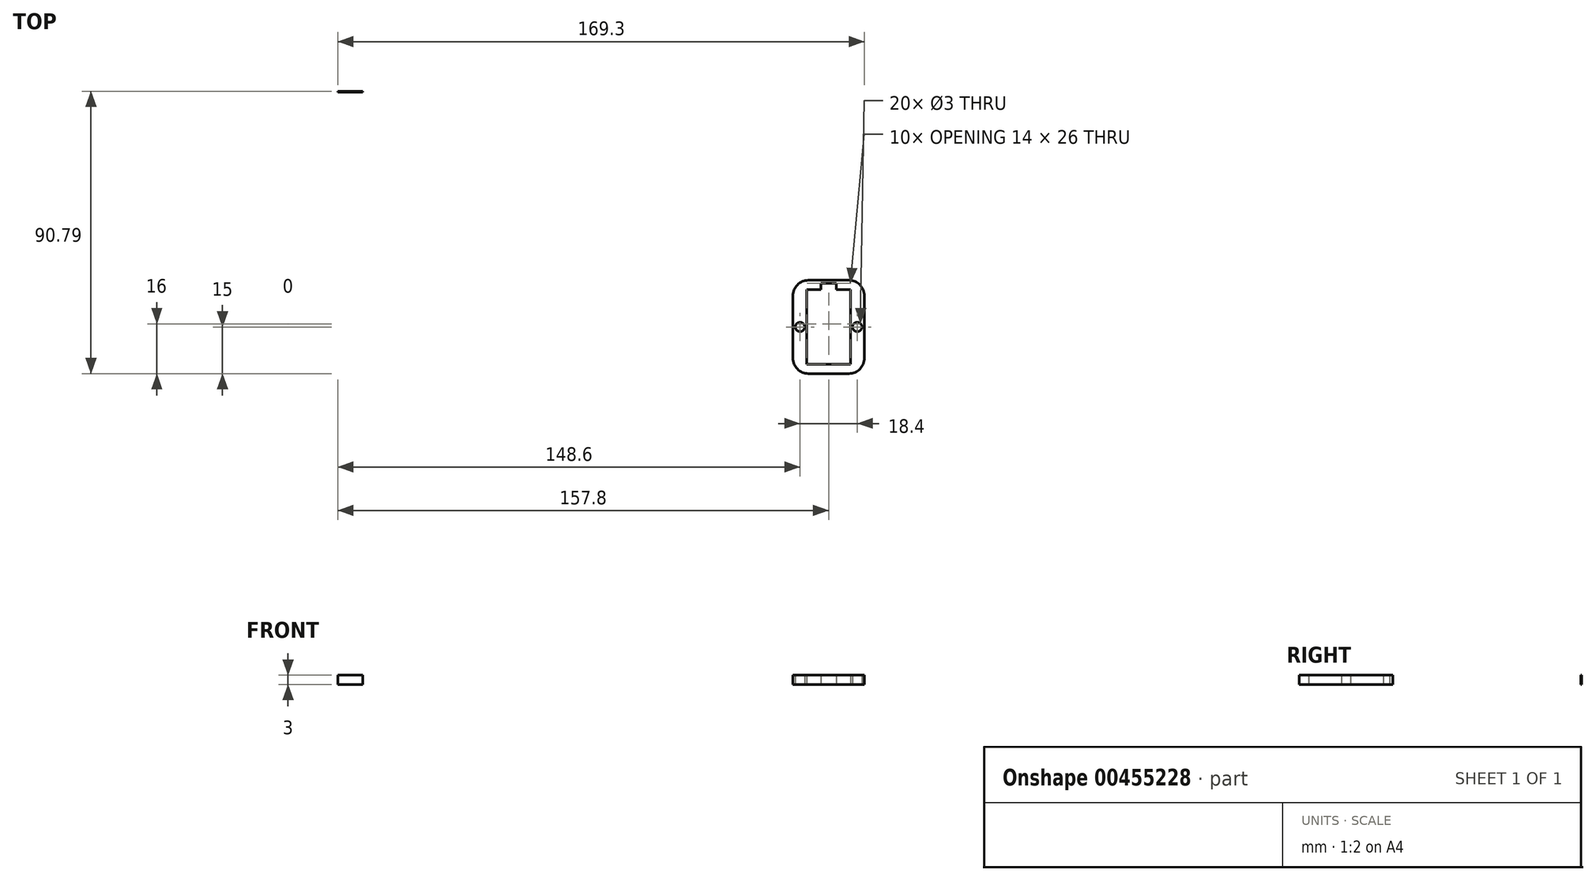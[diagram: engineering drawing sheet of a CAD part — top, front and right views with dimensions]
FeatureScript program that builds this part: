
annotation { "Feature Type Name" : "Feature", "Feature Type Description" : "" }
export const myFeature = defineFeature(function(context is Context, id is Id, definition is map)
    precondition{}
    {
        {
            var Q0;
            Q0=qCreatedBy(makeId("Top.planeOp"),FACE);
            var sketch = newSketch(context, id + "F0", { "sketchPlane" : qUnion([Q0])});
            skLineSegment(sketch, "E0.bottom", {"start": v(-157.8, 75.5) * mm, "end": v(-149.8, 75.5) * mm});
            skLineSegment(sketch, "E0.top", {"start": v(-157.8, 75.79) * mm, "end": v(-149.8, 75.79) * mm});
            skLineSegment(sketch, "E0.left", {"start": v(-157.8, 75.5) * mm, "end": v(-157.8, 75.79) * mm});
            skLineSegment(sketch, "E0.right", {"start": v(-149.8, 75.5) * mm, "end": v(-149.8, 75.79) * mm});
            skLineSegment(sketch, "E1.bottom", {"start": v(6.5, 15) * mm, "end": v(-6.5, 15) * mm});
            skLineSegment(sketch, "E1.top", {"start": v(6.5, -15) * mm, "end": v(-6.5, -15) * mm});
            skLineSegment(sketch, "E1.left", {"start": v(11.5, 10) * mm, "end": v(11.5, -10) * mm});
            skLineSegment(sketch, "E1.right", {"start": v(-11.5, 10) * mm, "end": v(-11.5, -10) * mm});
            skPoint(sketch, "E1.middle", {"position": v(0, 0) * mm});
            skLineSegment(sketch, "E2.bottom", {"start": v(7, 12) * mm, "end": v(-7, 12) * mm});
            skLineSegment(sketch, "E2.top", {"start": v(7, -12) * mm, "end": v(-7, -12) * mm});
            skLineSegment(sketch, "E2.left", {"start": v(7, 12) * mm, "end": v(7, -12) * mm});
            skLineSegment(sketch, "E2.right", {"start": v(-7, 12) * mm, "end": v(-7, -12) * mm});
            skLineSegment(sketch, "E3", {"start": v(-7, 12) * mm, "end": v(-2.5, 12) * mm});
            skLineSegment(sketch, "E4", {"start": v(-2.5, 12) * mm, "end": v(-2.5, 14) * mm});
            skLineSegment(sketch, "E5", {"start": v(-2.5, 14) * mm, "end": v(2.5, 14) * mm});
            skLineSegment(sketch, "E6", {"start": v(2.5, 14) * mm, "end": v(2.5, 12) * mm});
            skPoint(sketch, "E7.visualSharp", {"position": v(11.5, 15) * mm});
            skArc(sketch, "E7.filletArc", {"start": v(11.5, 10) * mm, "mid": v(10.04, 13.54) * mm, "end": v(6.5, 15) * mm});
            skPoint(sketch, "E8.visualSharp", {"position": v(11.5, -15) * mm});
            skArc(sketch, "E8.filletArc", {"start": v(6.5, -15) * mm, "mid": v(10.04, -13.54) * mm, "end": v(11.5, -10) * mm});
            skPoint(sketch, "E9.visualSharp", {"position": v(-11.5, -15) * mm});
            skArc(sketch, "E9.filletArc", {"start": v(-11.5, -10) * mm, "mid": v(-10.04, -13.54) * mm, "end": v(-6.5, -15) * mm});
            skPoint(sketch, "E10.visualSharp", {"position": v(-11.5, 15) * mm});
            skArc(sketch, "E10.filletArc", {"start": v(-6.5, 15) * mm, "mid": v(-10.04, 13.54) * mm, "end": v(-11.5, 10) * mm});
            skLineSegment(sketch, "E11", {"start": v(-11.5, 0) * mm, "end": v(-9.2, 0) * mm});
            skLineSegment(sketch, "E12", {"start": v(11.5, 0) * mm, "end": v(9.2, 0) * mm});
            skCircle(sketch, "E13", {"center": v(-9.2, 0) * mm, "radius": 1.5 * mm});
            skCircle(sketch, "E14", {"center": v(9.2, 0) * mm, "radius": 1.5 * mm});
            skSolve(sketch);
        }
        {
            var Q0;
            Q0 = qSketchRegion(id + "F0", true);
            extrude(context, id + "F1", {"entities" : qUnion([Q0]), "depth" : 3 * mm});
        }
    });
